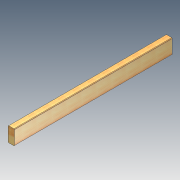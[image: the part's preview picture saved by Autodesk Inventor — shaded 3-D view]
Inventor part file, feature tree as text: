
AUTODESK INVENTOR PART (.ipt)
format: ipt  version: 2012 (Build 160160000, 160)  size: 83,456 bytes
history: native  units: in
note: dims shown in document units (in); Inventor stores cm internally (conversion verified against a paired STEP export)
features: extrude x1, sketch x1
ambient origin geometry x8: Origin, YZ Plane, XZ Plane, XY Plane, X Axis, Y Axis, Z Axis, Center Point
bodies: Solid1 (feature_tree)
feature tree (2):
  extrude  "Extrusion1"  Depth=1.5in
  sketch  "Sketch1"  dims[d0=3.5in d1=1.5in d2=0.125in d3=37.5in d4=0.0in]
